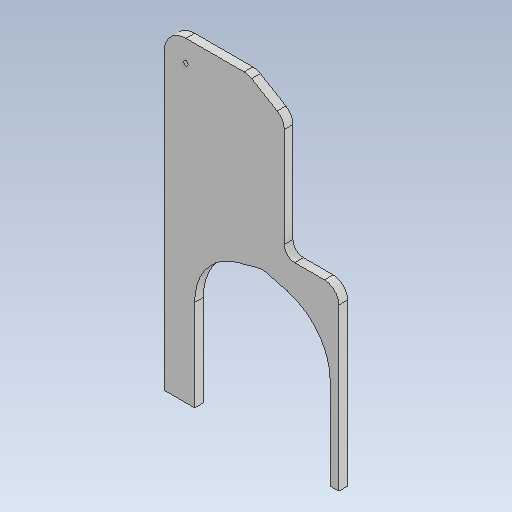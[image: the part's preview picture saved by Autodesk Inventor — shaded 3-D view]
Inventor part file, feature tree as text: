
AUTODESK INVENTOR PART (.ipt)
format: ipt  version: 2020 (Build 240168000, 168)  size: 137,216 bytes
history: native  units: mm
features: other x4, sketch x1
ambient origin geometry x8: Origin, YZ Plane, XZ Plane, XY Plane, X Axis, Y Axis, Z Axis, Center Point
bodies: Body1 (feature_tree)
feature tree (5):
  other  "guarra_MIR.ipt"
  other  "Sólido1::guarra_MIR.ipt"
  other  "OperaçãoIdentificador1"
  sketch  "Esboço1"  dims[d0=10.0mm]
  other  "Sólido1"
